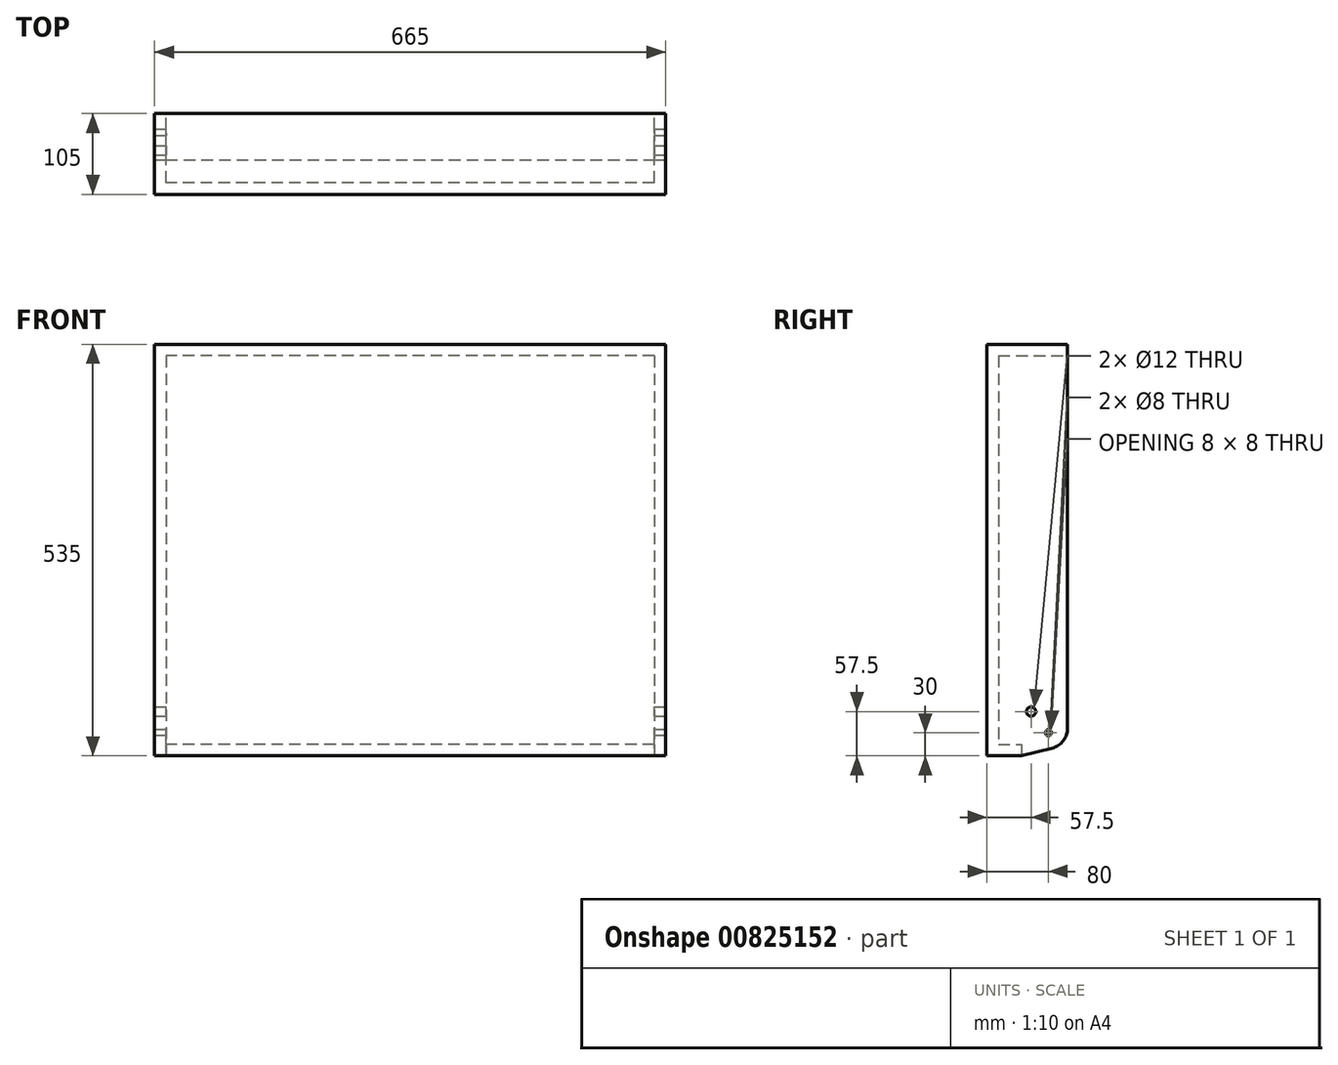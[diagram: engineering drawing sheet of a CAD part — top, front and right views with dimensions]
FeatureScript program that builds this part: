
annotation { "Feature Type Name" : "Feature", "Feature Type Description" : "" }
export const myFeature = defineFeature(function(context is Context, id is Id, definition is map)
    precondition{}
    {
        {
            var Q0;
            Q0=qCreatedBy(makeId("Front.planeOp"),FACE);
            var sketch = newSketch(context, id + "F0", { "sketchPlane" : qUnion([Q0])});
            skLineSegment(sketch, "E0.bottom", {"start": v(0, 535) * mm, "end": v(665, 535) * mm});
            skLineSegment(sketch, "E0.top", {"start": v(0, 0) * mm, "end": v(665, 0) * mm});
            skLineSegment(sketch, "E0.left", {"start": v(0, 535) * mm, "end": v(0, 0) * mm});
            skLineSegment(sketch, "E0.right", {"start": v(665, 535) * mm, "end": v(665, 0) * mm});
            skSolve(sketch);
        }
        {
            var Q0;
            Q0=makeQuery(id+"F0.imprint","IMPRINT",FACE,{"disambiguationData":[TD([[makeQuery(id+"F0.imprint","IMPRINT",EDGE,{"derivedFrom":sQuery(id+"F0.wireOp",EDGE,"E0.bottom")}),-1.0]])]});
            extrude(context, id + "F1", {"entities" : qUnion([Q0]), "oppositeDirection" : true, "depth" : 105 * mm, "offsetDistance" : 25 * mm});
        }
        {
            var Q0;
            Q0=makeQuery(id+"F1.opExtrude","CAP_FACE",FACE,{"disambiguationData":[OSD([sQuery(id+"F0.wireOp",EDGE,"E0.bottom"),sQuery(id+"F0.wireOp",EDGE,"E0.top"),sQuery(id+"F0.wireOp",EDGE,"E0.left"),sQuery(id+"F0.wireOp",EDGE,"E0.right")])],"isStart":false});
            var sketch = newSketch(context, id + "F2", { "sketchPlane" : qUnion([Q0])});
            skLineSegment(sketch, "E1.bottom", {"start": v(-650, 520) * mm, "end": v(-15, 520) * mm});
            skLineSegment(sketch, "E1.top", {"start": v(-650, 15) * mm, "end": v(-15, 15) * mm});
            skLineSegment(sketch, "E1.left", {"start": v(-650, 520) * mm, "end": v(-650, 15) * mm});
            skLineSegment(sketch, "E1.right", {"start": v(-15, 520) * mm, "end": v(-15, 15) * mm});
            skSolve(sketch);
        }
        {
            var Q0;
            Q0=makeQuery(id+"F2.imprint","IMPRINT",FACE,{"disambiguationData":[TD([[makeQuery(id+"F2.imprint","IMPRINT",EDGE,{"derivedFrom":sQuery(id+"F2.wireOp",EDGE,"E1.bottom")}),-1.0]])]});
            extrude(context, id + "F3", {"entities" : qUnion([Q0]), "operationType" : NewBodyOperationType.REMOVE, "endBound" : BoundingType.UP_TO_NEXT, "oppositeDirection" : true, "depth" : 100 * mm, "hasOffset" : true, "offsetDistance" : 15 * mm});
        }
        {
            var Q0;
            Q0=makeQuery(id+"F1.opExtrude","SWEPT_FACE",FACE,{"disambiguationData":[OSD([sQuery(id+"F0.wireOp",EDGE,"E0.right")])]});
            var sketch = newSketch(context, id + "F4", { "sketchPlane" : qUnion([Q0])});
            skPoint(sketch, "E2", {"position": v(57.5, 57.5) * mm});
            skSolve(sketch);
        }
        {
            var Q0;
            Q0=sQuery(id+"F4.wireOp",VERTEX,"E2");
            var Q1;
            Q1=makeQuery(id+"F1.opExtrude","SWEPT_BODY",BODY,{"disambiguationData":[OSD([sQuery(id+"F0.wireOp",EDGE,"E0.bottom"),sQuery(id+"F0.wireOp",EDGE,"E0.top"),sQuery(id+"F0.wireOp",EDGE,"E0.left"),sQuery(id+"F0.wireOp",EDGE,"E0.right")])]});
            hole(context, id + "F5", {"style" : HoleStyle.SIMPLE, "endStyle" : HoleEndStyle.THROUGH, "holeDiameter" : 12 * mm, "majorDiameter" : 5 * mm, "isTappedThrough" : true, "tappedDepth" : 12 * mm, "tapClearance" : 3, "locations" : qUnion([Q0]), "scope" : qUnion([Q1])});
        }
        {
            var Q0;
            Q0=makeQuery(id+"F1.opExtrude","CAP_FACE",FACE,{"disambiguationData":[OSD([sQuery(id+"F0.wireOp",EDGE,"E0.bottom"),sQuery(id+"F0.wireOp",EDGE,"E0.top"),sQuery(id+"F0.wireOp",EDGE,"E0.left"),sQuery(id+"F0.wireOp",EDGE,"E0.right")])],"isStart":false});
            var sketch = newSketch(context, id + "F6", { "sketchPlane" : qUnion([Q0])});
            skLineSegment(sketch, "E3.bottom", {"start": v(-650, 15) * mm, "end": v(-15, 15) * mm});
            skLineSegment(sketch, "E3.top", {"start": v(-650, 0) * mm, "end": v(-15, 0) * mm});
            skLineSegment(sketch, "E3.left", {"start": v(-650, 15) * mm, "end": v(-650, 0) * mm});
            skLineSegment(sketch, "E3.right", {"start": v(-15, 15) * mm, "end": v(-15, 0) * mm});
            skSolve(sketch);
        }
        {
            var Q0;
            Q0=makeQuery(id+"F6.imprint","IMPRINT",FACE,{"disambiguationData":[TD([[makeQuery(id+"F6.imprint","IMPRINT",EDGE,{"derivedFrom":sQuery(id+"F6.wireOp",EDGE,"E3.bottom")}),-1.0]])]});
            extrude(context, id + "F7", {"entities" : qUnion([Q0]), "operationType" : NewBodyOperationType.REMOVE, "oppositeDirection" : true, "depth" : 60 * mm, "offsetDistance" : 25 * mm});
        }
        {
            var Q0;
            {var subQ0=sQuery(id+"F0.wireOp",EDGE,"E0.right");var subQ1=sQuery(id+"F0.wireOp",EDGE,"E0.top");Q0=makeQuery(id+"F7.boolean.opBoolean","SPLIT",EDGE,{"disambiguationData":[TD([makeQuery(id+"F1.opExtrude","SWEPT_FACE",FACE,{"disambiguationData":[OSD([subQ0])]})])],"derivedFrom":makeQuery(id+"F1.opExtrude","CAP_EDGE",EDGE,{"disambiguationData":[OSD([subQ1])],"isStart":false})});}
            var Q1;
            {var subQ0=sQuery(id+"F0.wireOp",EDGE,"E0.left");var subQ1=sQuery(id+"F0.wireOp",EDGE,"E0.top");Q1=makeQuery(id+"F7.boolean.opBoolean","SPLIT",EDGE,{"disambiguationData":[TD([makeQuery(id+"F1.opExtrude","SWEPT_FACE",FACE,{"disambiguationData":[OSD([subQ0])]})])],"derivedFrom":makeQuery(id+"F1.opExtrude","CAP_EDGE",EDGE,{"disambiguationData":[OSD([subQ1])],"isStart":false})});}
            chamfer(context, id + "F8", {"entities" : qUnion([Q0, Q1]), "chamferType" : ChamferType.TWO_OFFSETS, "width1" : 60 * mm, "oppositeDirection" : false, "width2" : 15 * mm, "tangentPropagation" : true});
        }
        {
            var Q0;
            {var subQ0=sQuery(id+"F0.wireOp",EDGE,"E0.right");var subQ1=sQuery(id+"F0.wireOp",EDGE,"E0.top");var subQ2=makeQuery(id+"F1.opExtrude","CAP_FACE",FACE,{"disambiguationData":[OSD([sQuery(id+"F0.wireOp",EDGE,"E0.bottom"),subQ1,sQuery(id+"F0.wireOp",EDGE,"E0.left"),subQ0])],"isStart":false});Q0=makeQuery(id+"F8.opChamfer","BLEND_EDGE",EDGE,{"blendedFrom":[makeQuery(id+"F7.boolean.opBoolean","SPLIT",EDGE,{"disambiguationData":[TD([makeQuery(id+"F1.opExtrude","SWEPT_FACE",FACE,{"disambiguationData":[OSD([subQ0])]})])],"derivedFrom":makeQuery(id+"F1.opExtrude","CAP_EDGE",EDGE,{"disambiguationData":[OSD([subQ1])],"isStart":false})}),subQ2],"blendedInto":[subQ2]});}
            var Q1;
            {var subQ0=sQuery(id+"F0.wireOp",EDGE,"E0.left");var subQ1=sQuery(id+"F0.wireOp",EDGE,"E0.top");var subQ2=makeQuery(id+"F1.opExtrude","CAP_FACE",FACE,{"disambiguationData":[OSD([sQuery(id+"F0.wireOp",EDGE,"E0.bottom"),subQ1,subQ0,sQuery(id+"F0.wireOp",EDGE,"E0.right")])],"isStart":false});Q1=makeQuery(id+"F8.opChamfer","BLEND_EDGE",EDGE,{"blendedFrom":[makeQuery(id+"F7.boolean.opBoolean","SPLIT",EDGE,{"disambiguationData":[TD([makeQuery(id+"F1.opExtrude","SWEPT_FACE",FACE,{"disambiguationData":[OSD([subQ0])]})])],"derivedFrom":makeQuery(id+"F1.opExtrude","CAP_EDGE",EDGE,{"disambiguationData":[OSD([subQ1])],"isStart":false})}),subQ2],"blendedInto":[subQ2]});}
            fillet(context, id + "F9", {"entities" : qUnion([Q0, Q1]), "radius" : 27 * mm, "tangentPropagation" : true, "allowEdgeOverflow" : false});
        }
        {
            var Q0;
            Q0=makeQuery(id+"F1.opExtrude","SWEPT_FACE",FACE,{"disambiguationData":[OSD([sQuery(id+"F0.wireOp",EDGE,"E0.left")])]});
            var sketch = newSketch(context, id + "F10", { "sketchPlane" : qUnion([Q0])});
            skPoint(sketch, "E4", {"position": v(-80, 30) * mm});
            skSolve(sketch);
        }
        {
            var Q0;
            Q0=sQuery(id+"F10.wireOp",VERTEX,"E4");
            var Q1;
            Q1=makeQuery(id+"F1.opExtrude","SWEPT_BODY",BODY,{"disambiguationData":[OSD([sQuery(id+"F0.wireOp",EDGE,"E0.bottom"),sQuery(id+"F0.wireOp",EDGE,"E0.top"),sQuery(id+"F0.wireOp",EDGE,"E0.left"),sQuery(id+"F0.wireOp",EDGE,"E0.right")])]});
            hole(context, id + "F11", {"style" : HoleStyle.SIMPLE, "endStyle" : HoleEndStyle.THROUGH, "holeDiameter" : 8 * mm, "majorDiameter" : 5 * mm, "isTappedThrough" : true, "tappedDepth" : 12 * mm, "tapClearance" : 3, "locations" : qUnion([Q0]), "scope" : qUnion([Q1])});
        }
    });
